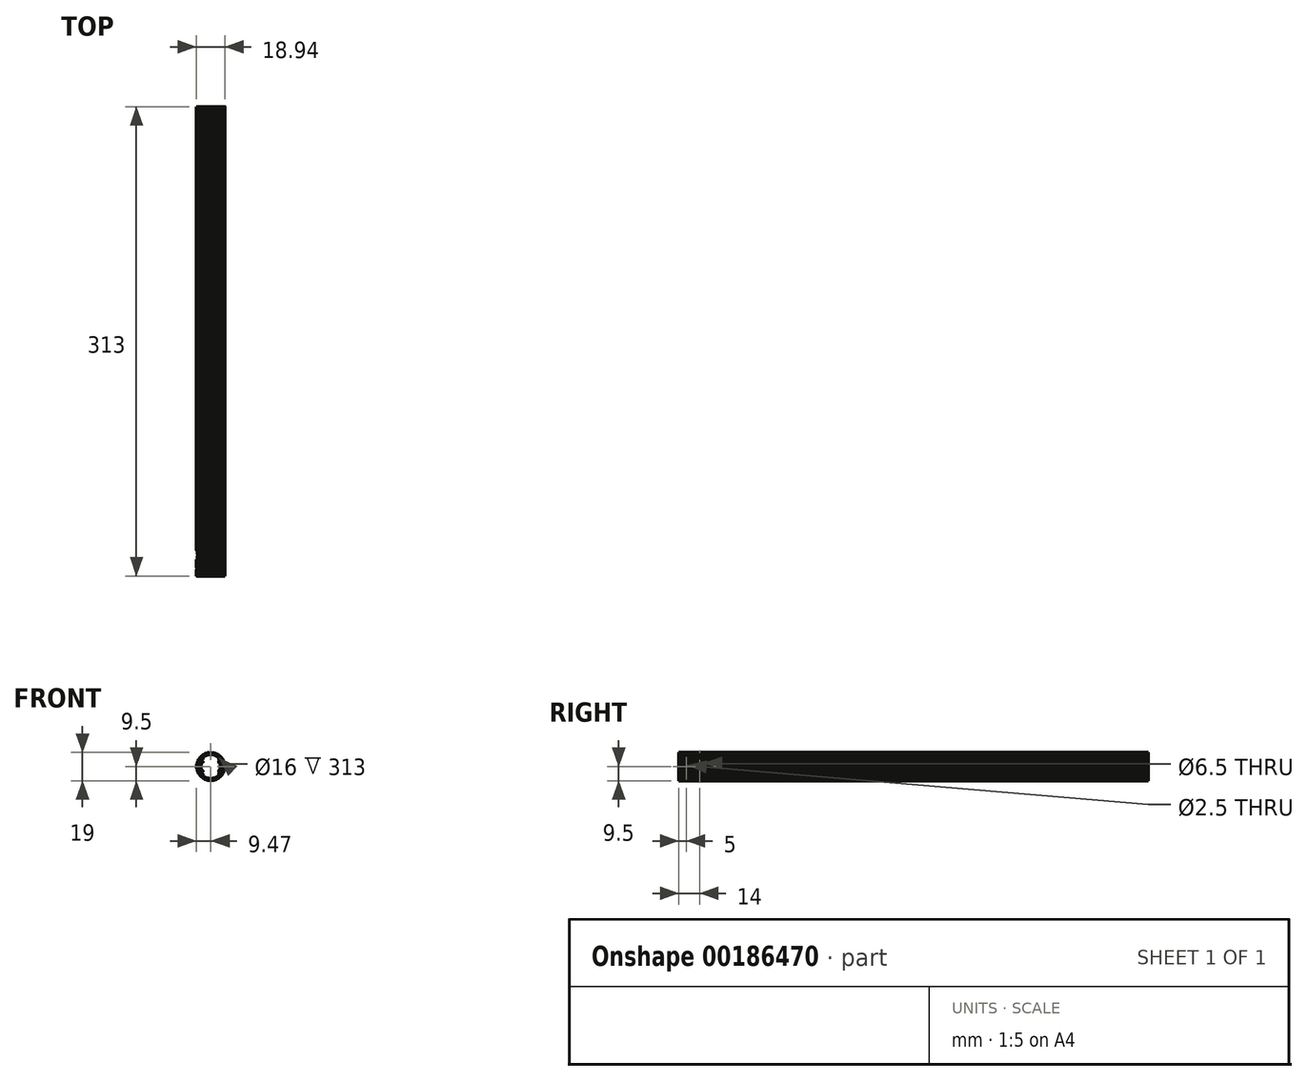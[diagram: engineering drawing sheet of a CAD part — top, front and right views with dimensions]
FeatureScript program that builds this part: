
annotation { "Feature Type Name" : "Feature", "Feature Type Description" : "" }
export const myFeature = defineFeature(function(context is Context, id is Id, definition is map)
    precondition{}
    {
        {
            assignVariable(context, id + "F0", {"name" : "Main_Diam", "anyValue" : 19});
        }
        {
            assignVariable(context, id + "F1", {"name" : "Main_Length", "anyValue" : 313});
        }
        {
            assignVariable(context, id + "F2", {"name" : "Bore_Depth_F", "anyValue" : 61});
        }
        {
            assignVariable(context, id + "F3", {"name" : "Bore_Depth_R", "anyValue" : 31});
        }
        {
            var Q0;
            Q0=qCreatedBy(makeId("Front.planeOp"),FACE);
            var sketch = newSketch(context, id + "F4", { "sketchPlane" : qUnion([Q0])});
            skLineSegment(sketch, "E0", {"start": v(-5.25, -3.45) * mm, "end": v(-5.25, -2.65) * mm});
            skLineSegment(sketch, "E1", {"start": v(9.2, 1.38) * mm, "end": v(9.42, 1.2) * mm});
            skArc(sketch, "E2", {"start": v(-5.35, -2.55) * mm, "mid": v(-5.28, -2.58) * mm, "end": v(-5.25, -2.65) * mm});
            skArc(sketch, "E3", {"start": v(6.3, 4.75) * mm, "mid": v(6.37, 4.72) * mm, "end": v(6.4, 4.65) * mm});
            skArc(sketch, "E4", {"start": v(-5.25, -6.04) * mm, "mid": v(0, -8) * mm, "end": v(5.25, -6.04) * mm});
            skLineSegment(sketch, "E5", {"start": v(1.53, 9.17) * mm, "end": v(1.78, 9.33) * mm});
            skLineSegment(sketch, "E6", {"start": v(-7.18, -5.91) * mm, "end": v(-7.2, -6.2) * mm});
            skArc(sketch, "E7", {"start": v(-8.33, -4.58) * mm, "mid": v(-8.23, -4.75) * mm, "end": v(-8.13, -4.92) * mm});
            skLineSegment(sketch, "E8", {"start": v(5.13, 7.76) * mm, "end": v(5.42, 7.8) * mm});
            skLineSegment(sketch, "E9", {"start": v(6.4, -2.45) * mm, "end": v(6.4, 0) * mm});
            skLineSegment(sketch, "E10", {"start": v(-2.33, -9) * mm, "end": v(-2.17, -9.25) * mm});
            skArc(sketch, "E11", {"start": v(8.97, -3.13) * mm, "mid": v(9.04, -2.94) * mm, "end": v(9.1, -2.74) * mm});
            skArc(sketch, "E12", {"start": v(-4.05, -8.6) * mm, "mid": v(-3.86, -8.68) * mm, "end": v(-3.68, -8.76) * mm});
            skArc(sketch, "E13", {"start": v(4.05, 8.6) * mm, "mid": v(3.86, 8.68) * mm, "end": v(3.68, 8.76) * mm});
            skLineSegment(sketch, "E14", {"start": v(6.63, 6.52) * mm, "end": v(6.92, 6.5) * mm});
            skArc(sketch, "E15", {"start": v(-6.4, 3.65) * mm, "mid": v(-6.37, 3.58) * mm, "end": v(-6.3, 3.55) * mm});
            skArc(sketch, "E16", {"start": v(5.74, 7.57) * mm, "mid": v(5.58, 7.69) * mm, "end": v(5.42, 7.8) * mm});
            skLineSegment(sketch, "E17", {"start": v(-9.2, 1.38) * mm, "end": v(-9.42, 1.2) * mm});
            skArc(sketch, "E18", {"start": v(1.78, -9.33) * mm, "mid": v(1.98, -9.3) * mm, "end": v(2.17, -9.25) * mm});
            skLineSegment(sketch, "E19", {"start": v(-5.8, 7.28) * mm, "end": v(-5.74, 7.57) * mm});
            skArc(sketch, "E20", {"start": v(-2.17, -9.25) * mm, "mid": v(-1.98, -9.3) * mm, "end": v(-1.78, -9.33) * mm});
            skLineSegment(sketch, "E21", {"start": v(7.84, 5) * mm, "end": v(8.13, 4.92) * mm});
            skLineSegment(sketch, "E22", {"start": v(2.33, 9) * mm, "end": v(2.17, 9.25) * mm});
            skArc(sketch, "E23", {"start": v(5.25, -3.45) * mm, "mid": v(5.28, -3.52) * mm, "end": v(5.35, -3.55) * mm});
            skLineSegment(sketch, "E24", {"start": v(5.8, -7.28) * mm, "end": v(5.74, -7.57) * mm});
            skArc(sketch, "E25", {"start": v(5.35, 2.55) * mm, "mid": v(5.28, 2.58) * mm, "end": v(5.25, 2.65) * mm});
            skArc(sketch, "E26", {"start": v(4.15, -8.32) * mm, "mid": v(4.65, -8.05) * mm, "end": v(5.13, -7.76) * mm});
            skArc(sketch, "E27", {"start": v(-5.35, 4.75) * mm, "mid": v(-5.28, 4.78) * mm, "end": v(-5.25, 4.85) * mm});
            skArc(sketch, "E28", {"start": v(-8.13, 4.92) * mm, "mid": v(-8.23, 4.75) * mm, "end": v(-8.33, 4.58) * mm});
            skLineSegment(sketch, "E29", {"start": v(7.84, -5) * mm, "end": v(8.13, -4.92) * mm});
            skArc(sketch, "E30", {"start": v(8.33, 4.58) * mm, "mid": v(8.23, 4.75) * mm, "end": v(8.13, 4.92) * mm});
            skLineSegment(sketch, "E31", {"start": v(-6.3, 3.55) * mm, "end": v(-5.35, 3.55) * mm});
            skLineSegment(sketch, "E32", {"start": v(-5.25, 3.45) * mm, "end": v(-5.25, 2.65) * mm});
            skArc(sketch, "E33", {"start": v(9.1, 2.74) * mm, "mid": v(9.04, 2.94) * mm, "end": v(8.97, 3.13) * mm});
            skLineSegment(sketch, "E34", {"start": v(6.3, 3.55) * mm, "end": v(5.35, 3.55) * mm});
            skLineSegment(sketch, "E35", {"start": v(4.15, -8.32) * mm, "end": v(4.05, -8.6) * mm});
            skLineSegment(sketch, "E36", {"start": v(5.25, 6.04) * mm, "end": v(5.25, 4.85) * mm});
            skArc(sketch, "E37", {"start": v(8.71, 3.26) * mm, "mid": v(8.5, 3.78) * mm, "end": v(8.25, 4.3) * mm});
            skArc(sketch, "E38", {"start": v(0.4, -9.3) * mm, "mid": v(0.97, -9.25) * mm, "end": v(1.53, -9.17) * mm});
            skArc(sketch, "E39", {"start": v(9.47, 0.8) * mm, "mid": v(9.45, 1) * mm, "end": v(9.42, 1.2) * mm});
            skArc(sketch, "E40", {"start": v(-4.15, 8.32) * mm, "mid": v(-4.65, 8.05) * mm, "end": v(-5.13, 7.76) * mm});
            skLineSegment(sketch, "E41", {"start": v(-0.4, 9.3) * mm, "end": v(-0.2, 9.5) * mm});
            skLineSegment(sketch, "E42", {"start": v(8.25, 4.3) * mm, "end": v(8.33, 4.58) * mm});
            skLineSegment(sketch, "E43", {"start": v(2.33, -9) * mm, "end": v(2.17, -9.25) * mm});
            skArc(sketch, "E44", {"start": v(-0.4, 9.3) * mm, "mid": v(-0.97, 9.25) * mm, "end": v(-1.53, 9.17) * mm});
            skLineSegment(sketch, "E45", {"start": v(-5.13, 7.76) * mm, "end": v(-5.42, 7.8) * mm});
            skLineSegment(sketch, "E46", {"start": v(-2.33, 9) * mm, "end": v(-2.17, 9.25) * mm});
            skLineSegment(sketch, "E47", {"start": v(6.63, -6.52) * mm, "end": v(6.92, -6.5) * mm});
            skArc(sketch, "E48", {"start": v(9.42, -1.2) * mm, "mid": v(9.45, -1) * mm, "end": v(9.47, -0.8) * mm});
            skArc(sketch, "E49", {"start": v(-3.68, 8.76) * mm, "mid": v(-3.86, 8.68) * mm, "end": v(-4.05, 8.6) * mm});
            skArc(sketch, "E50", {"start": v(9.2, 1.38) * mm, "mid": v(9.1, 1.93) * mm, "end": v(8.96, 2.48) * mm});
            skArc(sketch, "E51", {"start": v(5.35, 4.75) * mm, "mid": v(5.28, 4.78) * mm, "end": v(5.25, 4.85) * mm});
            skLineSegment(sketch, "E52", {"start": v(5.25, 3.45) * mm, "end": v(5.25, 2.65) * mm});
            skArc(sketch, "E53", {"start": v(-0.2, -9.5) * mm, "mid": v(0, -9.5) * mm, "end": v(0.2, -9.5) * mm});
            skArc(sketch, "E54", {"start": v(7.2, 6.2) * mm, "mid": v(7.06, 6.36) * mm, "end": v(6.92, 6.5) * mm});
            skLineSegment(sketch, "E55", {"start": v(3.4, 8.65) * mm, "end": v(3.68, 8.76) * mm});
            skArc(sketch, "E56", {"start": v(6.4, 3.65) * mm, "mid": v(6.37, 3.58) * mm, "end": v(6.3, 3.55) * mm});
            skLineSegment(sketch, "E57", {"start": v(-6.4, -2.45) * mm, "end": v(-6.4, 0) * mm});
            skArc(sketch, "E58", {"start": v(-2.33, 9) * mm, "mid": v(-2.87, 8.84) * mm, "end": v(-3.4, 8.65) * mm});
            skLineSegment(sketch, "E59", {"start": v(-1.53, 9.17) * mm, "end": v(-1.78, 9.33) * mm});
            skLineSegment(sketch, "E60", {"start": v(0.4, -9.3) * mm, "end": v(0.2, -9.5) * mm});
            skArc(sketch, "E61", {"start": v(-6.92, 6.5) * mm, "mid": v(-7.06, 6.36) * mm, "end": v(-7.2, 6.2) * mm});
            skArc(sketch, "E62", {"start": v(-8.25, 4.3) * mm, "mid": v(-8.5, 3.78) * mm, "end": v(-8.71, 3.26) * mm});
            skArc(sketch, "E63", {"start": v(6.3, -4.75) * mm, "mid": v(6.37, -4.72) * mm, "end": v(6.4, -4.65) * mm});
            skLineSegment(sketch, "E64", {"start": v(-6.4, 4.65) * mm, "end": v(-6.4, 3.65) * mm});
            skLineSegment(sketch, "E65", {"start": v(-6.4, 2.45) * mm, "end": v(-6.4, 0) * mm});
            skArc(sketch, "E66", {"start": v(8.25, -4.3) * mm, "mid": v(8.5, -3.78) * mm, "end": v(8.71, -3.26) * mm});
            skArc(sketch, "E67", {"start": v(-6.3, 2.55) * mm, "mid": v(-6.37, 2.52) * mm, "end": v(-6.4, 2.45) * mm});
            skLineSegment(sketch, "E68", {"start": v(-5.25, 6.04) * mm, "end": v(-5.25, 4.85) * mm});
            skLineSegment(sketch, "E69", {"start": v(-5.35, 4.75) * mm, "end": v(-6.3, 4.75) * mm});
            skLineSegment(sketch, "E70", {"start": v(-5.35, 2.55) * mm, "end": v(-6.3, 2.55) * mm});
            skArc(sketch, "E71", {"start": v(-5.25, 3.45) * mm, "mid": v(-5.28, 3.52) * mm, "end": v(-5.35, 3.55) * mm});
            skArc(sketch, "E72", {"start": v(-5.35, 2.55) * mm, "mid": v(-5.28, 2.58) * mm, "end": v(-5.25, 2.65) * mm});
            skArc(sketch, "E73", {"start": v(-6.3, 4.75) * mm, "mid": v(-6.37, 4.72) * mm, "end": v(-6.4, 4.65) * mm});
            skArc(sketch, "E74", {"start": v(6.3, 2.55) * mm, "mid": v(6.37, 2.52) * mm, "end": v(6.4, 2.45) * mm});
            skLineSegment(sketch, "E75", {"start": v(5.35, 2.55) * mm, "end": v(6.3, 2.55) * mm});
            skArc(sketch, "E76", {"start": v(5.25, 3.45) * mm, "mid": v(5.28, 3.52) * mm, "end": v(5.35, 3.55) * mm});
            skArc(sketch, "E77", {"start": v(0.2, 9.5) * mm, "mid": v(0, 9.5) * mm, "end": v(-0.2, 9.5) * mm});
            skLineSegment(sketch, "E78", {"start": v(5.35, 4.75) * mm, "end": v(6.3, 4.75) * mm});
            skLineSegment(sketch, "E79", {"start": v(6.4, 2.45) * mm, "end": v(6.4, 0) * mm});
            skLineSegment(sketch, "E80", {"start": v(6.4, 4.65) * mm, "end": v(6.4, 3.65) * mm});
            skArc(sketch, "E81", {"start": v(-5.35, -4.75) * mm, "mid": v(-5.28, -4.78) * mm, "end": v(-5.25, -4.85) * mm});
            skLineSegment(sketch, "E82", {"start": v(-6.3, -3.55) * mm, "end": v(-5.35, -3.55) * mm});
            skLineSegment(sketch, "E83", {"start": v(-5.35, -2.55) * mm, "end": v(-6.3, -2.55) * mm});
            skArc(sketch, "E84", {"start": v(-5.25, -3.45) * mm, "mid": v(-5.28, -3.52) * mm, "end": v(-5.35, -3.55) * mm});
            skArc(sketch, "E85", {"start": v(-6.3, -2.55) * mm, "mid": v(-6.37, -2.52) * mm, "end": v(-6.4, -2.45) * mm});
            skArc(sketch, "E86", {"start": v(-6.4, -3.65) * mm, "mid": v(-6.37, -3.58) * mm, "end": v(-6.3, -3.55) * mm});
            skArc(sketch, "E87", {"start": v(-6.3, -4.75) * mm, "mid": v(-6.37, -4.72) * mm, "end": v(-6.4, -4.65) * mm});
            skArc(sketch, "E88", {"start": v(5.35, -2.55) * mm, "mid": v(5.28, -2.58) * mm, "end": v(5.25, -2.65) * mm});
            skLineSegment(sketch, "E89", {"start": v(-3.4, 8.65) * mm, "end": v(-3.68, 8.76) * mm});
            skArc(sketch, "E90", {"start": v(6.3, -2.55) * mm, "mid": v(6.37, -2.52) * mm, "end": v(6.4, -2.45) * mm});
            skLineSegment(sketch, "E91", {"start": v(5.35, -2.55) * mm, "end": v(6.3, -2.55) * mm});
            skArc(sketch, "E92", {"start": v(6.4, -3.65) * mm, "mid": v(6.37, -3.58) * mm, "end": v(6.3, -3.55) * mm});
            skLineSegment(sketch, "E93", {"start": v(6.3, -3.55) * mm, "end": v(5.35, -3.55) * mm});
            skArc(sketch, "E94", {"start": v(5.35, -4.75) * mm, "mid": v(5.28, -4.78) * mm, "end": v(5.25, -4.85) * mm});
            skLineSegment(sketch, "E95", {"start": v(-5.25, -6.04) * mm, "end": v(-5.25, -4.85) * mm});
            skLineSegment(sketch, "E96", {"start": v(5.25, -3.45) * mm, "end": v(5.25, -2.65) * mm});
            skLineSegment(sketch, "E97", {"start": v(6.4, -4.65) * mm, "end": v(6.4, -3.65) * mm});
            skLineSegment(sketch, "E98", {"start": v(-5.35, -4.75) * mm, "end": v(-6.3, -4.75) * mm});
            skArc(sketch, "E99", {"start": v(-8.97, 3.13) * mm, "mid": v(-9.04, 2.94) * mm, "end": v(-9.1, 2.74) * mm});
            skLineSegment(sketch, "E100", {"start": v(-6.4, -4.65) * mm, "end": v(-6.4, -3.65) * mm});
            skLineSegment(sketch, "E101", {"start": v(5.35, -4.75) * mm, "end": v(6.3, -4.75) * mm});
            skLineSegment(sketch, "E102", {"start": v(-7.84, 5) * mm, "end": v(-8.13, 4.92) * mm});
            skLineSegment(sketch, "E103", {"start": v(5.25, -6.04) * mm, "end": v(5.25, -4.85) * mm});
            skArc(sketch, "E104", {"start": v(5.25, 6.04) * mm, "mid": v(0, 8) * mm, "end": v(-5.25, 6.04) * mm});
            skLineSegment(sketch, "E105", {"start": v(-0.4, -9.3) * mm, "end": v(-0.2, -9.5) * mm});
            skArc(sketch, "E106", {"start": v(2.33, -9) * mm, "mid": v(2.87, -8.84) * mm, "end": v(3.4, -8.65) * mm});
            skLineSegment(sketch, "E107", {"start": v(1.53, -9.17) * mm, "end": v(1.78, -9.33) * mm});
            skArc(sketch, "E108", {"start": v(3.68, -8.76) * mm, "mid": v(3.86, -8.68) * mm, "end": v(4.05, -8.6) * mm});
            skArc(sketch, "E109", {"start": v(-9.1, -2.74) * mm, "mid": v(-9.04, -2.94) * mm, "end": v(-8.97, -3.13) * mm});
            skLineSegment(sketch, "E110", {"start": v(3.4, -8.65) * mm, "end": v(3.68, -8.76) * mm});
            skArc(sketch, "E111", {"start": v(5.8, -7.28) * mm, "mid": v(6.22, -6.91) * mm, "end": v(6.63, -6.52) * mm});
            skArc(sketch, "E112", {"start": v(5.42, -7.8) * mm, "mid": v(5.58, -7.69) * mm, "end": v(5.74, -7.57) * mm});
            skLineSegment(sketch, "E113", {"start": v(5.13, -7.76) * mm, "end": v(5.42, -7.8) * mm});
            skLineSegment(sketch, "E114", {"start": v(-5.13, -7.76) * mm, "end": v(-5.42, -7.8) * mm});
            skLineSegment(sketch, "E115", {"start": v(7.18, -5.91) * mm, "end": v(7.2, -6.2) * mm});
            skLineSegment(sketch, "E116", {"start": v(-6.63, -6.52) * mm, "end": v(-6.92, -6.5) * mm});
            skArc(sketch, "E117", {"start": v(8.13, -4.92) * mm, "mid": v(8.23, -4.75) * mm, "end": v(8.33, -4.58) * mm});
            skArc(sketch, "E118", {"start": v(6.92, -6.5) * mm, "mid": v(7.06, -6.36) * mm, "end": v(7.2, -6.2) * mm});
            skArc(sketch, "E119", {"start": v(-5.74, -7.57) * mm, "mid": v(-5.58, -7.69) * mm, "end": v(-5.42, -7.8) * mm});
            skArc(sketch, "E120", {"start": v(8.96, -2.48) * mm, "mid": v(9.1, -1.93) * mm, "end": v(9.2, -1.38) * mm});
            skLineSegment(sketch, "E121", {"start": v(8.96, -2.48) * mm, "end": v(9.1, -2.74) * mm});
            skLineSegment(sketch, "E122", {"start": v(8.71, -3.26) * mm, "end": v(8.97, -3.13) * mm});
            skArc(sketch, "E123", {"start": v(9.28, -0.57) * mm, "mid": v(9.3, 0) * mm, "end": v(9.28, 0.57) * mm});
            skLineSegment(sketch, "E124", {"start": v(9.28, -0.57) * mm, "end": v(9.47, -0.8) * mm});
            skLineSegment(sketch, "E125", {"start": v(-1.53, -9.17) * mm, "end": v(-1.78, -9.33) * mm});
            skLineSegment(sketch, "E126", {"start": v(9.2, -1.38) * mm, "end": v(9.42, -1.2) * mm});
            skLineSegment(sketch, "E127", {"start": v(8.71, 3.26) * mm, "end": v(8.97, 3.13) * mm});
            skLineSegment(sketch, "E128", {"start": v(8.96, 2.48) * mm, "end": v(9.1, 2.74) * mm});
            skArc(sketch, "E129", {"start": v(7.84, 5) * mm, "mid": v(7.52, 5.47) * mm, "end": v(7.18, 5.91) * mm});
            skArc(sketch, "E130", {"start": v(6.63, 6.52) * mm, "mid": v(6.22, 6.91) * mm, "end": v(5.8, 7.28) * mm});
            skLineSegment(sketch, "E131", {"start": v(7.18, 5.91) * mm, "end": v(7.2, 6.2) * mm});
            skArc(sketch, "E132", {"start": v(5.13, 7.76) * mm, "mid": v(4.65, 8.05) * mm, "end": v(4.15, 8.32) * mm});
            skLineSegment(sketch, "E133", {"start": v(5.8, 7.28) * mm, "end": v(5.74, 7.57) * mm});
            skArc(sketch, "E134", {"start": v(3.4, 8.65) * mm, "mid": v(2.87, 8.84) * mm, "end": v(2.33, 9) * mm});
            skLineSegment(sketch, "E135", {"start": v(4.15, 8.32) * mm, "end": v(4.05, 8.6) * mm});
            skArc(sketch, "E136", {"start": v(1.53, 9.17) * mm, "mid": v(0.97, 9.25) * mm, "end": v(0.4, 9.3) * mm});
            skArc(sketch, "E137", {"start": v(2.17, 9.25) * mm, "mid": v(1.98, 9.3) * mm, "end": v(1.78, 9.33) * mm});
            skLineSegment(sketch, "E138", {"start": v(0.4, 9.3) * mm, "end": v(0.2, 9.5) * mm});
            skArc(sketch, "E139", {"start": v(-1.78, 9.33) * mm, "mid": v(-1.98, 9.3) * mm, "end": v(-2.17, 9.25) * mm});
            skLineSegment(sketch, "E140", {"start": v(-4.15, 8.32) * mm, "end": v(-4.05, 8.6) * mm});
            skArc(sketch, "E141", {"start": v(-5.8, 7.28) * mm, "mid": v(-6.22, 6.91) * mm, "end": v(-6.63, 6.52) * mm});
            skArc(sketch, "E142", {"start": v(-5.42, 7.8) * mm, "mid": v(-5.58, 7.69) * mm, "end": v(-5.74, 7.57) * mm});
            skLineSegment(sketch, "E143", {"start": v(-9.2, -1.38) * mm, "end": v(-9.42, -1.2) * mm});
            skLineSegment(sketch, "E144", {"start": v(-7.18, 5.91) * mm, "end": v(-7.2, 6.2) * mm});
            skLineSegment(sketch, "E145", {"start": v(-6.63, 6.52) * mm, "end": v(-6.92, 6.5) * mm});
            skArc(sketch, "E146", {"start": v(-8.96, 2.48) * mm, "mid": v(-9.1, 1.93) * mm, "end": v(-9.2, 1.38) * mm});
            skLineSegment(sketch, "E147", {"start": v(-8.96, 2.48) * mm, "end": v(-9.1, 2.74) * mm});
            skLineSegment(sketch, "E148", {"start": v(-8.71, 3.26) * mm, "end": v(-8.97, 3.13) * mm});
            skArc(sketch, "E149", {"start": v(-9.28, 0.57) * mm, "mid": v(-9.3, 0) * mm, "end": v(-9.28, -0.57) * mm});
            skArc(sketch, "E150", {"start": v(-9.42, 1.2) * mm, "mid": v(-9.45, 1) * mm, "end": v(-9.47, 0.8) * mm});
            skLineSegment(sketch, "E151", {"start": v(-9.28, 0.57) * mm, "end": v(-9.47, 0.8) * mm});
            skLineSegment(sketch, "E152", {"start": v(8.25, -4.3) * mm, "end": v(8.33, -4.58) * mm});
            skArc(sketch, "E153", {"start": v(-9.2, -1.38) * mm, "mid": v(-9.1, -1.93) * mm, "end": v(-8.96, -2.48) * mm});
            skArc(sketch, "E154", {"start": v(-9.47, -0.8) * mm, "mid": v(-9.45, -1) * mm, "end": v(-9.42, -1.2) * mm});
            skLineSegment(sketch, "E155", {"start": v(-9.28, -0.57) * mm, "end": v(-9.47, -0.8) * mm});
            skArc(sketch, "E156", {"start": v(-8.71, -3.26) * mm, "mid": v(-8.5, -3.78) * mm, "end": v(-8.25, -4.3) * mm});
            skLineSegment(sketch, "E157", {"start": v(-8.71, -3.26) * mm, "end": v(-8.97, -3.13) * mm});
            skLineSegment(sketch, "E158", {"start": v(-8.96, -2.48) * mm, "end": v(-9.1, -2.74) * mm});
            skArc(sketch, "E159", {"start": v(-7.84, -5) * mm, "mid": v(-7.52, -5.47) * mm, "end": v(-7.18, -5.91) * mm});
            skLineSegment(sketch, "E160", {"start": v(-7.84, -5) * mm, "end": v(-8.13, -4.92) * mm});
            skLineSegment(sketch, "E161", {"start": v(-8.25, -4.3) * mm, "end": v(-8.33, -4.58) * mm});
            skArc(sketch, "E162", {"start": v(-6.63, -6.52) * mm, "mid": v(-6.22, -6.91) * mm, "end": v(-5.8, -7.28) * mm});
            skLineSegment(sketch, "E163", {"start": v(9.28, 0.57) * mm, "end": v(9.47, 0.8) * mm});
            skArc(sketch, "E164", {"start": v(-7.2, -6.2) * mm, "mid": v(-7.06, -6.36) * mm, "end": v(-6.92, -6.5) * mm});
            skArc(sketch, "E165", {"start": v(7.18, -5.91) * mm, "mid": v(7.52, -5.47) * mm, "end": v(7.84, -5) * mm});
            skLineSegment(sketch, "E166", {"start": v(-5.8, -7.28) * mm, "end": v(-5.74, -7.57) * mm});
            skArc(sketch, "E167", {"start": v(-3.4, -8.65) * mm, "mid": v(-2.87, -8.84) * mm, "end": v(-2.33, -9) * mm});
            skLineSegment(sketch, "E168", {"start": v(-3.4, -8.65) * mm, "end": v(-3.68, -8.76) * mm});
            skLineSegment(sketch, "E169", {"start": v(-4.15, -8.32) * mm, "end": v(-4.05, -8.6) * mm});
            skArc(sketch, "E170", {"start": v(-1.53, -9.17) * mm, "mid": v(-0.97, -9.25) * mm, "end": v(-0.4, -9.3) * mm});
            skArc(sketch, "E171", {"start": v(-7.18, 5.91) * mm, "mid": v(-7.52, 5.47) * mm, "end": v(-7.84, 5) * mm});
            skLineSegment(sketch, "E172", {"start": v(-8.25, 4.3) * mm, "end": v(-8.33, 4.58) * mm});
            skArc(sketch, "E173", {"start": v(-5.13, -7.76) * mm, "mid": v(-4.65, -8.05) * mm, "end": v(-4.15, -8.32) * mm});
            skSolve(sketch);
        }
        {
            var Q0;
            Q0=makeQuery(id+"F4.imprint","IMPRINT",FACE,{"disambiguationData":[TD([[makeQuery(id+"F4.imprint","IMPRINT",EDGE,{"derivedFrom":sQuery(id+"F4.wireOp",EDGE,"E0")}),1.0]])]});
            extrude(context, id + "F5", {"entities" : qUnion([Q0]), "depth" : (getVariable(context, 'Main_Length') - getVariable(context, 'Bore_Depth_F') - getVariable(context, 'Bore_Depth_R')) * mm});
        }
        {
            var Q0;
            Q0=makeQuery(id+"F5.opExtrude","CAP_FACE",FACE,{"disambiguationData":[OSD([sQuery(id+"F4.wireOp",EDGE,"E0"),sQuery(id+"F4.wireOp",EDGE,"E1"),sQuery(id+"F4.wireOp",EDGE,"E2"),sQuery(id+"F4.wireOp",EDGE,"E3"),sQuery(id+"F4.wireOp",EDGE,"E4"),sQuery(id+"F4.wireOp",EDGE,"E5"),sQuery(id+"F4.wireOp",EDGE,"E6"),sQuery(id+"F4.wireOp",EDGE,"E7"),sQuery(id+"F4.wireOp",EDGE,"E8"),sQuery(id+"F4.wireOp",EDGE,"E9"),sQuery(id+"F4.wireOp",EDGE,"E10"),sQuery(id+"F4.wireOp",EDGE,"E11"),sQuery(id+"F4.wireOp",EDGE,"E12"),sQuery(id+"F4.wireOp",EDGE,"E13"),sQuery(id+"F4.wireOp",EDGE,"E14"),sQuery(id+"F4.wireOp",EDGE,"E15"),sQuery(id+"F4.wireOp",EDGE,"E16"),sQuery(id+"F4.wireOp",EDGE,"E17"),sQuery(id+"F4.wireOp",EDGE,"E18"),sQuery(id+"F4.wireOp",EDGE,"E19"),sQuery(id+"F4.wireOp",EDGE,"E20"),sQuery(id+"F4.wireOp",EDGE,"E21"),sQuery(id+"F4.wireOp",EDGE,"E22"),sQuery(id+"F4.wireOp",EDGE,"E23"),sQuery(id+"F4.wireOp",EDGE,"E24"),sQuery(id+"F4.wireOp",EDGE,"E25"),sQuery(id+"F4.wireOp",EDGE,"E26"),sQuery(id+"F4.wireOp",EDGE,"E27"),sQuery(id+"F4.wireOp",EDGE,"E28"),sQuery(id+"F4.wireOp",EDGE,"E29"),sQuery(id+"F4.wireOp",EDGE,"E30"),sQuery(id+"F4.wireOp",EDGE,"E31"),sQuery(id+"F4.wireOp",EDGE,"E32"),sQuery(id+"F4.wireOp",EDGE,"E33"),sQuery(id+"F4.wireOp",EDGE,"E34"),sQuery(id+"F4.wireOp",EDGE,"E35"),sQuery(id+"F4.wireOp",EDGE,"E36"),sQuery(id+"F4.wireOp",EDGE,"E37"),sQuery(id+"F4.wireOp",EDGE,"E38"),sQuery(id+"F4.wireOp",EDGE,"E39"),sQuery(id+"F4.wireOp",EDGE,"E40"),sQuery(id+"F4.wireOp",EDGE,"E41"),sQuery(id+"F4.wireOp",EDGE,"E42"),sQuery(id+"F4.wireOp",EDGE,"E43"),sQuery(id+"F4.wireOp",EDGE,"E44"),sQuery(id+"F4.wireOp",EDGE,"E45"),sQuery(id+"F4.wireOp",EDGE,"E46"),sQuery(id+"F4.wireOp",EDGE,"E47"),sQuery(id+"F4.wireOp",EDGE,"E48"),sQuery(id+"F4.wireOp",EDGE,"E49"),sQuery(id+"F4.wireOp",EDGE,"E50"),sQuery(id+"F4.wireOp",EDGE,"E51"),sQuery(id+"F4.wireOp",EDGE,"E52"),sQuery(id+"F4.wireOp",EDGE,"E53"),sQuery(id+"F4.wireOp",EDGE,"E54"),sQuery(id+"F4.wireOp",EDGE,"E55"),sQuery(id+"F4.wireOp",EDGE,"E56"),sQuery(id+"F4.wireOp",EDGE,"E57"),sQuery(id+"F4.wireOp",EDGE,"E58"),sQuery(id+"F4.wireOp",EDGE,"E59"),sQuery(id+"F4.wireOp",EDGE,"E60"),sQuery(id+"F4.wireOp",EDGE,"E61"),sQuery(id+"F4.wireOp",EDGE,"E62"),sQuery(id+"F4.wireOp",EDGE,"E63"),sQuery(id+"F4.wireOp",EDGE,"E64"),sQuery(id+"F4.wireOp",EDGE,"E65"),sQuery(id+"F4.wireOp",EDGE,"E66"),sQuery(id+"F4.wireOp",EDGE,"E67"),sQuery(id+"F4.wireOp",EDGE,"E68"),sQuery(id+"F4.wireOp",EDGE,"E69"),sQuery(id+"F4.wireOp",EDGE,"E70"),sQuery(id+"F4.wireOp",EDGE,"E71"),sQuery(id+"F4.wireOp",EDGE,"E72"),sQuery(id+"F4.wireOp",EDGE,"E73"),sQuery(id+"F4.wireOp",EDGE,"E74"),sQuery(id+"F4.wireOp",EDGE,"E75"),sQuery(id+"F4.wireOp",EDGE,"E76"),sQuery(id+"F4.wireOp",EDGE,"E77"),sQuery(id+"F4.wireOp",EDGE,"E78"),sQuery(id+"F4.wireOp",EDGE,"E79"),sQuery(id+"F4.wireOp",EDGE,"E80"),sQuery(id+"F4.wireOp",EDGE,"E81"),sQuery(id+"F4.wireOp",EDGE,"E82"),sQuery(id+"F4.wireOp",EDGE,"E83"),sQuery(id+"F4.wireOp",EDGE,"E84"),sQuery(id+"F4.wireOp",EDGE,"E85"),sQuery(id+"F4.wireOp",EDGE,"E86"),sQuery(id+"F4.wireOp",EDGE,"E87"),sQuery(id+"F4.wireOp",EDGE,"E88"),sQuery(id+"F4.wireOp",EDGE,"E89"),sQuery(id+"F4.wireOp",EDGE,"E90"),sQuery(id+"F4.wireOp",EDGE,"E91"),sQuery(id+"F4.wireOp",EDGE,"E92"),sQuery(id+"F4.wireOp",EDGE,"E93"),sQuery(id+"F4.wireOp",EDGE,"E94"),sQuery(id+"F4.wireOp",EDGE,"E95"),sQuery(id+"F4.wireOp",EDGE,"E96"),sQuery(id+"F4.wireOp",EDGE,"E97"),sQuery(id+"F4.wireOp",EDGE,"E98"),sQuery(id+"F4.wireOp",EDGE,"E99"),sQuery(id+"F4.wireOp",EDGE,"E100"),sQuery(id+"F4.wireOp",EDGE,"E101"),sQuery(id+"F4.wireOp",EDGE,"E102"),sQuery(id+"F4.wireOp",EDGE,"E103"),sQuery(id+"F4.wireOp",EDGE,"E104"),sQuery(id+"F4.wireOp",EDGE,"E105"),sQuery(id+"F4.wireOp",EDGE,"E106"),sQuery(id+"F4.wireOp",EDGE,"E107"),sQuery(id+"F4.wireOp",EDGE,"E108"),sQuery(id+"F4.wireOp",EDGE,"E109"),sQuery(id+"F4.wireOp",EDGE,"E110"),sQuery(id+"F4.wireOp",EDGE,"E111"),sQuery(id+"F4.wireOp",EDGE,"E112"),sQuery(id+"F4.wireOp",EDGE,"E113"),sQuery(id+"F4.wireOp",EDGE,"E114"),sQuery(id+"F4.wireOp",EDGE,"E115"),sQuery(id+"F4.wireOp",EDGE,"E116"),sQuery(id+"F4.wireOp",EDGE,"E117"),sQuery(id+"F4.wireOp",EDGE,"E118"),sQuery(id+"F4.wireOp",EDGE,"E119"),sQuery(id+"F4.wireOp",EDGE,"E120"),sQuery(id+"F4.wireOp",EDGE,"E121"),sQuery(id+"F4.wireOp",EDGE,"E122"),sQuery(id+"F4.wireOp",EDGE,"E123"),sQuery(id+"F4.wireOp",EDGE,"E124"),sQuery(id+"F4.wireOp",EDGE,"E125"),sQuery(id+"F4.wireOp",EDGE,"E126"),sQuery(id+"F4.wireOp",EDGE,"E127"),sQuery(id+"F4.wireOp",EDGE,"E128"),sQuery(id+"F4.wireOp",EDGE,"E129"),sQuery(id+"F4.wireOp",EDGE,"E130"),sQuery(id+"F4.wireOp",EDGE,"E131"),sQuery(id+"F4.wireOp",EDGE,"E132"),sQuery(id+"F4.wireOp",EDGE,"E133"),sQuery(id+"F4.wireOp",EDGE,"E134"),sQuery(id+"F4.wireOp",EDGE,"E135"),sQuery(id+"F4.wireOp",EDGE,"E136"),sQuery(id+"F4.wireOp",EDGE,"E137"),sQuery(id+"F4.wireOp",EDGE,"E138"),sQuery(id+"F4.wireOp",EDGE,"E139"),sQuery(id+"F4.wireOp",EDGE,"E140"),sQuery(id+"F4.wireOp",EDGE,"E141"),sQuery(id+"F4.wireOp",EDGE,"E142"),sQuery(id+"F4.wireOp",EDGE,"E143"),sQuery(id+"F4.wireOp",EDGE,"E144"),sQuery(id+"F4.wireOp",EDGE,"E145"),sQuery(id+"F4.wireOp",EDGE,"E146"),sQuery(id+"F4.wireOp",EDGE,"E147"),sQuery(id+"F4.wireOp",EDGE,"E148"),sQuery(id+"F4.wireOp",EDGE,"E149"),sQuery(id+"F4.wireOp",EDGE,"E150"),sQuery(id+"F4.wireOp",EDGE,"E151"),sQuery(id+"F4.wireOp",EDGE,"E152"),sQuery(id+"F4.wireOp",EDGE,"E153"),sQuery(id+"F4.wireOp",EDGE,"E154"),sQuery(id+"F4.wireOp",EDGE,"E155"),sQuery(id+"F4.wireOp",EDGE,"E156"),sQuery(id+"F4.wireOp",EDGE,"E157"),sQuery(id+"F4.wireOp",EDGE,"E158"),sQuery(id+"F4.wireOp",EDGE,"E159"),sQuery(id+"F4.wireOp",EDGE,"E160"),sQuery(id+"F4.wireOp",EDGE,"E161"),sQuery(id+"F4.wireOp",EDGE,"E162"),sQuery(id+"F4.wireOp",EDGE,"E163"),sQuery(id+"F4.wireOp",EDGE,"E164"),sQuery(id+"F4.wireOp",EDGE,"E165"),sQuery(id+"F4.wireOp",EDGE,"E166"),sQuery(id+"F4.wireOp",EDGE,"E167"),sQuery(id+"F4.wireOp",EDGE,"E168"),sQuery(id+"F4.wireOp",EDGE,"E169"),sQuery(id+"F4.wireOp",EDGE,"E170"),sQuery(id+"F4.wireOp",EDGE,"E171"),sQuery(id+"F4.wireOp",EDGE,"E172"),sQuery(id+"F4.wireOp",EDGE,"E173")])],"isStart":false});
            var sketch = newSketch(context, id + "F6", { "sketchPlane" : qUnion([Q0])});
            skCircle(sketch, "E174", {"center": v(0, 0) * mm, "radius": 8 * mm});
            skLineSegment(sketch, "E175.0.0", {"start": v(9.42, 1.2) * mm, "end": v(9.2, 1.38) * mm});
            skArc(sketch, "E175.0.1", {"start": v(9.2, 1.38) * mm, "mid": v(9.1, 1.93) * mm, "end": v(8.96, 2.48) * mm});
            skLineSegment(sketch, "E175.0.2", {"start": v(8.96, 2.48) * mm, "end": v(9.1, 2.74) * mm});
            skArc(sketch, "E175.0.3", {"start": v(9.1, 2.74) * mm, "mid": v(9.04, 2.94) * mm, "end": v(8.97, 3.13) * mm});
            skLineSegment(sketch, "E175.0.4", {"start": v(8.97, 3.13) * mm, "end": v(8.71, 3.26) * mm});
            skArc(sketch, "E175.0.5", {"start": v(8.71, 3.26) * mm, "mid": v(8.5, 3.78) * mm, "end": v(8.25, 4.3) * mm});
            skLineSegment(sketch, "E175.0.6", {"start": v(8.25, 4.3) * mm, "end": v(8.33, 4.58) * mm});
            skArc(sketch, "E175.0.7", {"start": v(8.33, 4.58) * mm, "mid": v(8.23, 4.75) * mm, "end": v(8.13, 4.92) * mm});
            skLineSegment(sketch, "E175.0.8", {"start": v(8.13, 4.92) * mm, "end": v(7.84, 5) * mm});
            skArc(sketch, "E175.0.9", {"start": v(7.84, 5) * mm, "mid": v(7.52, 5.47) * mm, "end": v(7.18, 5.91) * mm});
            skLineSegment(sketch, "E175.0.10", {"start": v(7.18, 5.91) * mm, "end": v(7.2, 6.2) * mm});
            skArc(sketch, "E175.0.11", {"start": v(7.2, 6.2) * mm, "mid": v(7.06, 6.36) * mm, "end": v(6.92, 6.5) * mm});
            skLineSegment(sketch, "E175.0.12", {"start": v(6.92, 6.5) * mm, "end": v(6.63, 6.52) * mm});
            skArc(sketch, "E175.0.13", {"start": v(6.63, 6.52) * mm, "mid": v(6.22, 6.91) * mm, "end": v(5.8, 7.28) * mm});
            skLineSegment(sketch, "E175.0.14", {"start": v(5.8, 7.28) * mm, "end": v(5.74, 7.57) * mm});
            skArc(sketch, "E175.0.15", {"start": v(5.74, 7.57) * mm, "mid": v(5.58, 7.69) * mm, "end": v(5.42, 7.8) * mm});
            skLineSegment(sketch, "E175.0.16", {"start": v(5.42, 7.8) * mm, "end": v(5.13, 7.76) * mm});
            skArc(sketch, "E175.0.17", {"start": v(5.13, 7.76) * mm, "mid": v(4.65, 8.05) * mm, "end": v(4.15, 8.32) * mm});
            skLineSegment(sketch, "E175.0.18", {"start": v(4.15, 8.32) * mm, "end": v(4.05, 8.6) * mm});
            skArc(sketch, "E175.0.19", {"start": v(4.05, 8.6) * mm, "mid": v(3.86, 8.68) * mm, "end": v(3.68, 8.76) * mm});
            skLineSegment(sketch, "E175.0.20", {"start": v(3.68, 8.76) * mm, "end": v(3.4, 8.65) * mm});
            skArc(sketch, "E175.0.21", {"start": v(3.4, 8.65) * mm, "mid": v(2.87, 8.84) * mm, "end": v(2.33, 9) * mm});
            skLineSegment(sketch, "E175.0.22", {"start": v(2.33, 9) * mm, "end": v(2.17, 9.25) * mm});
            skArc(sketch, "E175.0.23", {"start": v(2.17, 9.25) * mm, "mid": v(1.98, 9.3) * mm, "end": v(1.78, 9.33) * mm});
            skLineSegment(sketch, "E175.0.24", {"start": v(1.78, 9.33) * mm, "end": v(1.53, 9.17) * mm});
            skArc(sketch, "E175.0.25", {"start": v(1.53, 9.17) * mm, "mid": v(0.97, 9.25) * mm, "end": v(0.4, 9.3) * mm});
            skLineSegment(sketch, "E175.0.26", {"start": v(0.4, 9.3) * mm, "end": v(0.2, 9.5) * mm});
            skArc(sketch, "E175.0.27", {"start": v(0.2, 9.5) * mm, "mid": v(0, 9.5) * mm, "end": v(-0.2, 9.5) * mm});
            skLineSegment(sketch, "E175.0.28", {"start": v(-0.2, 9.5) * mm, "end": v(-0.4, 9.3) * mm});
            skArc(sketch, "E175.0.29", {"start": v(-0.4, 9.3) * mm, "mid": v(-0.97, 9.25) * mm, "end": v(-1.53, 9.17) * mm});
            skLineSegment(sketch, "E175.0.30", {"start": v(-1.53, 9.17) * mm, "end": v(-1.78, 9.33) * mm});
            skArc(sketch, "E175.0.31", {"start": v(-1.78, 9.33) * mm, "mid": v(-1.98, 9.3) * mm, "end": v(-2.17, 9.25) * mm});
            skLineSegment(sketch, "E175.0.32", {"start": v(-2.17, 9.25) * mm, "end": v(-2.33, 9) * mm});
            skArc(sketch, "E175.0.33", {"start": v(-2.33, 9) * mm, "mid": v(-2.87, 8.84) * mm, "end": v(-3.4, 8.65) * mm});
            skLineSegment(sketch, "E175.0.34", {"start": v(-3.4, 8.65) * mm, "end": v(-3.68, 8.76) * mm});
            skArc(sketch, "E175.0.35", {"start": v(-3.68, 8.76) * mm, "mid": v(-3.86, 8.68) * mm, "end": v(-4.05, 8.6) * mm});
            skLineSegment(sketch, "E175.0.36", {"start": v(-4.05, 8.6) * mm, "end": v(-4.15, 8.32) * mm});
            skArc(sketch, "E175.0.37", {"start": v(-4.15, 8.32) * mm, "mid": v(-4.65, 8.05) * mm, "end": v(-5.13, 7.76) * mm});
            skLineSegment(sketch, "E175.0.38", {"start": v(-5.13, 7.76) * mm, "end": v(-5.42, 7.8) * mm});
            skArc(sketch, "E175.0.39", {"start": v(-5.42, 7.8) * mm, "mid": v(-5.58, 7.69) * mm, "end": v(-5.74, 7.57) * mm});
            skLineSegment(sketch, "E175.0.40", {"start": v(-5.74, 7.57) * mm, "end": v(-5.8, 7.28) * mm});
            skArc(sketch, "E175.0.41", {"start": v(-5.8, 7.28) * mm, "mid": v(-6.22, 6.91) * mm, "end": v(-6.63, 6.52) * mm});
            skLineSegment(sketch, "E175.0.42", {"start": v(-6.63, 6.52) * mm, "end": v(-6.92, 6.5) * mm});
            skArc(sketch, "E175.0.43", {"start": v(-6.92, 6.5) * mm, "mid": v(-7.06, 6.36) * mm, "end": v(-7.2, 6.2) * mm});
            skLineSegment(sketch, "E175.0.44", {"start": v(-7.2, 6.2) * mm, "end": v(-7.18, 5.91) * mm});
            skArc(sketch, "E175.0.45", {"start": v(-7.18, 5.91) * mm, "mid": v(-7.52, 5.47) * mm, "end": v(-7.84, 5) * mm});
            skLineSegment(sketch, "E175.0.46", {"start": v(-7.84, 5) * mm, "end": v(-8.13, 4.92) * mm});
            skArc(sketch, "E175.0.47", {"start": v(-8.13, 4.92) * mm, "mid": v(-8.23, 4.75) * mm, "end": v(-8.33, 4.58) * mm});
            skLineSegment(sketch, "E175.0.48", {"start": v(-8.33, 4.58) * mm, "end": v(-8.25, 4.3) * mm});
            skArc(sketch, "E175.0.49", {"start": v(-8.25, 4.3) * mm, "mid": v(-8.5, 3.78) * mm, "end": v(-8.71, 3.26) * mm});
            skLineSegment(sketch, "E175.0.50", {"start": v(-8.71, 3.26) * mm, "end": v(-8.97, 3.13) * mm});
            skArc(sketch, "E175.0.51", {"start": v(-8.97, 3.13) * mm, "mid": v(-9.04, 2.94) * mm, "end": v(-9.1, 2.74) * mm});
            skLineSegment(sketch, "E175.0.52", {"start": v(-9.1, 2.74) * mm, "end": v(-8.96, 2.48) * mm});
            skArc(sketch, "E175.0.53", {"start": v(-8.96, 2.48) * mm, "mid": v(-9.1, 1.93) * mm, "end": v(-9.2, 1.38) * mm});
            skLineSegment(sketch, "E175.0.54", {"start": v(-9.2, 1.38) * mm, "end": v(-9.42, 1.2) * mm});
            skArc(sketch, "E175.0.55", {"start": v(-9.42, 1.2) * mm, "mid": v(-9.45, 1) * mm, "end": v(-9.47, 0.8) * mm});
            skLineSegment(sketch, "E175.0.56", {"start": v(-9.47, 0.8) * mm, "end": v(-9.28, 0.57) * mm});
            skArc(sketch, "E175.0.57", {"start": v(-9.28, 0.57) * mm, "mid": v(-9.3, 0) * mm, "end": v(-9.28, -0.57) * mm});
            skLineSegment(sketch, "E175.0.58", {"start": v(-9.28, -0.57) * mm, "end": v(-9.47, -0.8) * mm});
            skArc(sketch, "E175.0.59", {"start": v(-9.47, -0.8) * mm, "mid": v(-9.45, -1) * mm, "end": v(-9.42, -1.2) * mm});
            skLineSegment(sketch, "E175.0.60", {"start": v(-9.42, -1.2) * mm, "end": v(-9.2, -1.38) * mm});
            skArc(sketch, "E175.0.61", {"start": v(-9.2, -1.38) * mm, "mid": v(-9.1, -1.93) * mm, "end": v(-8.96, -2.48) * mm});
            skLineSegment(sketch, "E175.0.62", {"start": v(-8.96, -2.48) * mm, "end": v(-9.1, -2.74) * mm});
            skArc(sketch, "E175.0.63", {"start": v(-9.1, -2.74) * mm, "mid": v(-9.04, -2.94) * mm, "end": v(-8.97, -3.13) * mm});
            skLineSegment(sketch, "E175.0.64", {"start": v(-8.97, -3.13) * mm, "end": v(-8.71, -3.26) * mm});
            skArc(sketch, "E175.0.65", {"start": v(-8.71, -3.26) * mm, "mid": v(-8.5, -3.78) * mm, "end": v(-8.25, -4.3) * mm});
            skLineSegment(sketch, "E175.0.66", {"start": v(-8.25, -4.3) * mm, "end": v(-8.33, -4.58) * mm});
            skArc(sketch, "E175.0.67", {"start": v(-8.33, -4.58) * mm, "mid": v(-8.23, -4.75) * mm, "end": v(-8.13, -4.92) * mm});
            skLineSegment(sketch, "E175.0.68", {"start": v(-8.13, -4.92) * mm, "end": v(-7.84, -5) * mm});
            skArc(sketch, "E175.0.69", {"start": v(-7.84, -5) * mm, "mid": v(-7.52, -5.47) * mm, "end": v(-7.18, -5.91) * mm});
            skLineSegment(sketch, "E175.0.70", {"start": v(-7.18, -5.91) * mm, "end": v(-7.2, -6.2) * mm});
            skArc(sketch, "E175.0.71", {"start": v(-7.2, -6.2) * mm, "mid": v(-7.06, -6.36) * mm, "end": v(-6.92, -6.5) * mm});
            skLineSegment(sketch, "E175.0.72", {"start": v(-6.92, -6.5) * mm, "end": v(-6.63, -6.52) * mm});
            skArc(sketch, "E175.0.73", {"start": v(-6.63, -6.52) * mm, "mid": v(-6.22, -6.91) * mm, "end": v(-5.8, -7.28) * mm});
            skLineSegment(sketch, "E175.0.74", {"start": v(-5.8, -7.28) * mm, "end": v(-5.74, -7.57) * mm});
            skArc(sketch, "E175.0.75", {"start": v(-5.74, -7.57) * mm, "mid": v(-5.58, -7.69) * mm, "end": v(-5.42, -7.8) * mm});
            skLineSegment(sketch, "E175.0.76", {"start": v(-5.42, -7.8) * mm, "end": v(-5.13, -7.76) * mm});
            skArc(sketch, "E175.0.77", {"start": v(-5.13, -7.76) * mm, "mid": v(-4.65, -8.05) * mm, "end": v(-4.15, -8.32) * mm});
            skLineSegment(sketch, "E175.0.78", {"start": v(-4.15, -8.32) * mm, "end": v(-4.05, -8.6) * mm});
            skArc(sketch, "E175.0.79", {"start": v(-4.05, -8.6) * mm, "mid": v(-3.86, -8.68) * mm, "end": v(-3.68, -8.76) * mm});
            skLineSegment(sketch, "E175.0.80", {"start": v(-3.68, -8.76) * mm, "end": v(-3.4, -8.65) * mm});
            skArc(sketch, "E175.0.81", {"start": v(-3.4, -8.65) * mm, "mid": v(-2.87, -8.84) * mm, "end": v(-2.33, -9) * mm});
            skLineSegment(sketch, "E175.0.82", {"start": v(-2.33, -9) * mm, "end": v(-2.17, -9.25) * mm});
            skArc(sketch, "E175.0.83", {"start": v(-2.17, -9.25) * mm, "mid": v(-1.98, -9.3) * mm, "end": v(-1.78, -9.33) * mm});
            skLineSegment(sketch, "E175.0.84", {"start": v(-1.78, -9.33) * mm, "end": v(-1.53, -9.17) * mm});
            skArc(sketch, "E175.0.85", {"start": v(-1.53, -9.17) * mm, "mid": v(-0.97, -9.25) * mm, "end": v(-0.4, -9.3) * mm});
            skLineSegment(sketch, "E175.0.86", {"start": v(-0.4, -9.3) * mm, "end": v(-0.2, -9.5) * mm});
            skArc(sketch, "E175.0.87", {"start": v(-0.2, -9.5) * mm, "mid": v(0, -9.5) * mm, "end": v(0.2, -9.5) * mm});
            skLineSegment(sketch, "E175.0.88", {"start": v(0.2, -9.5) * mm, "end": v(0.4, -9.3) * mm});
            skArc(sketch, "E175.0.89", {"start": v(0.4, -9.3) * mm, "mid": v(0.97, -9.25) * mm, "end": v(1.53, -9.17) * mm});
            skLineSegment(sketch, "E175.0.90", {"start": v(1.53, -9.17) * mm, "end": v(1.78, -9.33) * mm});
            skArc(sketch, "E175.0.91", {"start": v(1.78, -9.33) * mm, "mid": v(1.98, -9.3) * mm, "end": v(2.17, -9.25) * mm});
            skLineSegment(sketch, "E175.0.92", {"start": v(2.17, -9.25) * mm, "end": v(2.33, -9) * mm});
            skArc(sketch, "E175.0.93", {"start": v(2.33, -9) * mm, "mid": v(2.87, -8.84) * mm, "end": v(3.4, -8.65) * mm});
            skLineSegment(sketch, "E175.0.94", {"start": v(3.4, -8.65) * mm, "end": v(3.68, -8.76) * mm});
            skArc(sketch, "E175.0.95", {"start": v(3.68, -8.76) * mm, "mid": v(3.86, -8.68) * mm, "end": v(4.05, -8.6) * mm});
            skLineSegment(sketch, "E175.0.96", {"start": v(4.05, -8.6) * mm, "end": v(4.15, -8.32) * mm});
            skArc(sketch, "E175.0.97", {"start": v(4.15, -8.32) * mm, "mid": v(4.65, -8.05) * mm, "end": v(5.13, -7.76) * mm});
            skLineSegment(sketch, "E175.0.98", {"start": v(5.13, -7.76) * mm, "end": v(5.42, -7.8) * mm});
            skArc(sketch, "E175.0.99", {"start": v(5.42, -7.8) * mm, "mid": v(5.58, -7.69) * mm, "end": v(5.74, -7.57) * mm});
            skLineSegment(sketch, "E175.0.100", {"start": v(5.74, -7.57) * mm, "end": v(5.8, -7.28) * mm});
            skArc(sketch, "E175.0.101", {"start": v(5.8, -7.28) * mm, "mid": v(6.22, -6.91) * mm, "end": v(6.63, -6.52) * mm});
            skLineSegment(sketch, "E175.0.102", {"start": v(6.63, -6.52) * mm, "end": v(6.92, -6.5) * mm});
            skArc(sketch, "E175.0.103", {"start": v(6.92, -6.5) * mm, "mid": v(7.06, -6.36) * mm, "end": v(7.2, -6.2) * mm});
            skLineSegment(sketch, "E175.0.104", {"start": v(7.2, -6.2) * mm, "end": v(7.18, -5.91) * mm});
            skArc(sketch, "E175.0.105", {"start": v(7.18, -5.91) * mm, "mid": v(7.52, -5.47) * mm, "end": v(7.84, -5) * mm});
            skLineSegment(sketch, "E175.0.106", {"start": v(7.84, -5) * mm, "end": v(8.13, -4.92) * mm});
            skArc(sketch, "E175.0.107", {"start": v(8.13, -4.92) * mm, "mid": v(8.23, -4.75) * mm, "end": v(8.33, -4.58) * mm});
            skLineSegment(sketch, "E175.0.108", {"start": v(8.33, -4.58) * mm, "end": v(8.25, -4.3) * mm});
            skArc(sketch, "E175.0.109", {"start": v(8.25, -4.3) * mm, "mid": v(8.5, -3.78) * mm, "end": v(8.71, -3.26) * mm});
            skLineSegment(sketch, "E175.0.110", {"start": v(8.71, -3.26) * mm, "end": v(8.97, -3.13) * mm});
            skArc(sketch, "E175.0.111", {"start": v(8.97, -3.13) * mm, "mid": v(9.04, -2.94) * mm, "end": v(9.1, -2.74) * mm});
            skLineSegment(sketch, "E175.0.112", {"start": v(9.1, -2.74) * mm, "end": v(8.96, -2.48) * mm});
            skArc(sketch, "E175.0.113", {"start": v(8.96, -2.48) * mm, "mid": v(9.1, -1.93) * mm, "end": v(9.2, -1.38) * mm});
            skLineSegment(sketch, "E175.0.114", {"start": v(9.2, -1.38) * mm, "end": v(9.42, -1.2) * mm});
            skArc(sketch, "E175.0.115", {"start": v(9.42, -1.2) * mm, "mid": v(9.45, -1) * mm, "end": v(9.47, -0.8) * mm});
            skLineSegment(sketch, "E175.0.116", {"start": v(9.47, -0.8) * mm, "end": v(9.28, -0.57) * mm});
            skArc(sketch, "E175.0.117", {"start": v(9.28, -0.57) * mm, "mid": v(9.3, 0) * mm, "end": v(9.28, 0.57) * mm});
            skLineSegment(sketch, "E175.0.118", {"start": v(9.28, 0.57) * mm, "end": v(9.47, 0.8) * mm});
            skArc(sketch, "E175.0.119", {"start": v(9.47, 0.8) * mm, "mid": v(9.45, 1) * mm, "end": v(9.42, 1.2) * mm});
            skSolve(sketch);
        }
        {
            var Q0;
            Q0=makeQuery(id+"F6.imprint","IMPRINT",FACE,{"disambiguationData":[TD([[makeQuery(id+"F6.imprint","IMPRINT",EDGE,{"derivedFrom":sQuery(id+"F6.wireOp",EDGE,"E175.0.0")}),-1.0]])]});
            extrude(context, id + "F7", {"entities" : qUnion([Q0]), "operationType" : NewBodyOperationType.ADD, "depth" : (getVariable(context, 'Bore_Depth_F')) * mm});
        }
        {
            var Q0;
            Q0=makeQuery(id+"F5.opExtrude","CAP_FACE",FACE,{"disambiguationData":[OSD([sQuery(id+"F4.wireOp",EDGE,"E0"),sQuery(id+"F4.wireOp",EDGE,"E1"),sQuery(id+"F4.wireOp",EDGE,"E2"),sQuery(id+"F4.wireOp",EDGE,"E3"),sQuery(id+"F4.wireOp",EDGE,"E4"),sQuery(id+"F4.wireOp",EDGE,"E5"),sQuery(id+"F4.wireOp",EDGE,"E6"),sQuery(id+"F4.wireOp",EDGE,"E7"),sQuery(id+"F4.wireOp",EDGE,"E8"),sQuery(id+"F4.wireOp",EDGE,"E9"),sQuery(id+"F4.wireOp",EDGE,"E10"),sQuery(id+"F4.wireOp",EDGE,"E11"),sQuery(id+"F4.wireOp",EDGE,"E12"),sQuery(id+"F4.wireOp",EDGE,"E13"),sQuery(id+"F4.wireOp",EDGE,"E14"),sQuery(id+"F4.wireOp",EDGE,"E15"),sQuery(id+"F4.wireOp",EDGE,"E16"),sQuery(id+"F4.wireOp",EDGE,"E17"),sQuery(id+"F4.wireOp",EDGE,"E18"),sQuery(id+"F4.wireOp",EDGE,"E19"),sQuery(id+"F4.wireOp",EDGE,"E20"),sQuery(id+"F4.wireOp",EDGE,"E21"),sQuery(id+"F4.wireOp",EDGE,"E22"),sQuery(id+"F4.wireOp",EDGE,"E23"),sQuery(id+"F4.wireOp",EDGE,"E24"),sQuery(id+"F4.wireOp",EDGE,"E25"),sQuery(id+"F4.wireOp",EDGE,"E26"),sQuery(id+"F4.wireOp",EDGE,"E27"),sQuery(id+"F4.wireOp",EDGE,"E28"),sQuery(id+"F4.wireOp",EDGE,"E29"),sQuery(id+"F4.wireOp",EDGE,"E30"),sQuery(id+"F4.wireOp",EDGE,"E31"),sQuery(id+"F4.wireOp",EDGE,"E32"),sQuery(id+"F4.wireOp",EDGE,"E33"),sQuery(id+"F4.wireOp",EDGE,"E34"),sQuery(id+"F4.wireOp",EDGE,"E35"),sQuery(id+"F4.wireOp",EDGE,"E36"),sQuery(id+"F4.wireOp",EDGE,"E37"),sQuery(id+"F4.wireOp",EDGE,"E38"),sQuery(id+"F4.wireOp",EDGE,"E39"),sQuery(id+"F4.wireOp",EDGE,"E40"),sQuery(id+"F4.wireOp",EDGE,"E41"),sQuery(id+"F4.wireOp",EDGE,"E42"),sQuery(id+"F4.wireOp",EDGE,"E43"),sQuery(id+"F4.wireOp",EDGE,"E44"),sQuery(id+"F4.wireOp",EDGE,"E45"),sQuery(id+"F4.wireOp",EDGE,"E46"),sQuery(id+"F4.wireOp",EDGE,"E47"),sQuery(id+"F4.wireOp",EDGE,"E48"),sQuery(id+"F4.wireOp",EDGE,"E49"),sQuery(id+"F4.wireOp",EDGE,"E50"),sQuery(id+"F4.wireOp",EDGE,"E51"),sQuery(id+"F4.wireOp",EDGE,"E52"),sQuery(id+"F4.wireOp",EDGE,"E53"),sQuery(id+"F4.wireOp",EDGE,"E54"),sQuery(id+"F4.wireOp",EDGE,"E55"),sQuery(id+"F4.wireOp",EDGE,"E56"),sQuery(id+"F4.wireOp",EDGE,"E57"),sQuery(id+"F4.wireOp",EDGE,"E58"),sQuery(id+"F4.wireOp",EDGE,"E59"),sQuery(id+"F4.wireOp",EDGE,"E60"),sQuery(id+"F4.wireOp",EDGE,"E61"),sQuery(id+"F4.wireOp",EDGE,"E62"),sQuery(id+"F4.wireOp",EDGE,"E63"),sQuery(id+"F4.wireOp",EDGE,"E64"),sQuery(id+"F4.wireOp",EDGE,"E65"),sQuery(id+"F4.wireOp",EDGE,"E66"),sQuery(id+"F4.wireOp",EDGE,"E67"),sQuery(id+"F4.wireOp",EDGE,"E68"),sQuery(id+"F4.wireOp",EDGE,"E69"),sQuery(id+"F4.wireOp",EDGE,"E70"),sQuery(id+"F4.wireOp",EDGE,"E71"),sQuery(id+"F4.wireOp",EDGE,"E72"),sQuery(id+"F4.wireOp",EDGE,"E73"),sQuery(id+"F4.wireOp",EDGE,"E74"),sQuery(id+"F4.wireOp",EDGE,"E75"),sQuery(id+"F4.wireOp",EDGE,"E76"),sQuery(id+"F4.wireOp",EDGE,"E77"),sQuery(id+"F4.wireOp",EDGE,"E78"),sQuery(id+"F4.wireOp",EDGE,"E79"),sQuery(id+"F4.wireOp",EDGE,"E80"),sQuery(id+"F4.wireOp",EDGE,"E81"),sQuery(id+"F4.wireOp",EDGE,"E82"),sQuery(id+"F4.wireOp",EDGE,"E83"),sQuery(id+"F4.wireOp",EDGE,"E84"),sQuery(id+"F4.wireOp",EDGE,"E85"),sQuery(id+"F4.wireOp",EDGE,"E86"),sQuery(id+"F4.wireOp",EDGE,"E87"),sQuery(id+"F4.wireOp",EDGE,"E88"),sQuery(id+"F4.wireOp",EDGE,"E89"),sQuery(id+"F4.wireOp",EDGE,"E90"),sQuery(id+"F4.wireOp",EDGE,"E91"),sQuery(id+"F4.wireOp",EDGE,"E92"),sQuery(id+"F4.wireOp",EDGE,"E93"),sQuery(id+"F4.wireOp",EDGE,"E94"),sQuery(id+"F4.wireOp",EDGE,"E95"),sQuery(id+"F4.wireOp",EDGE,"E96"),sQuery(id+"F4.wireOp",EDGE,"E97"),sQuery(id+"F4.wireOp",EDGE,"E98"),sQuery(id+"F4.wireOp",EDGE,"E99"),sQuery(id+"F4.wireOp",EDGE,"E100"),sQuery(id+"F4.wireOp",EDGE,"E101"),sQuery(id+"F4.wireOp",EDGE,"E102"),sQuery(id+"F4.wireOp",EDGE,"E103"),sQuery(id+"F4.wireOp",EDGE,"E104"),sQuery(id+"F4.wireOp",EDGE,"E105"),sQuery(id+"F4.wireOp",EDGE,"E106"),sQuery(id+"F4.wireOp",EDGE,"E107"),sQuery(id+"F4.wireOp",EDGE,"E108"),sQuery(id+"F4.wireOp",EDGE,"E109"),sQuery(id+"F4.wireOp",EDGE,"E110"),sQuery(id+"F4.wireOp",EDGE,"E111"),sQuery(id+"F4.wireOp",EDGE,"E112"),sQuery(id+"F4.wireOp",EDGE,"E113"),sQuery(id+"F4.wireOp",EDGE,"E114"),sQuery(id+"F4.wireOp",EDGE,"E115"),sQuery(id+"F4.wireOp",EDGE,"E116"),sQuery(id+"F4.wireOp",EDGE,"E117"),sQuery(id+"F4.wireOp",EDGE,"E118"),sQuery(id+"F4.wireOp",EDGE,"E119"),sQuery(id+"F4.wireOp",EDGE,"E120"),sQuery(id+"F4.wireOp",EDGE,"E121"),sQuery(id+"F4.wireOp",EDGE,"E122"),sQuery(id+"F4.wireOp",EDGE,"E123"),sQuery(id+"F4.wireOp",EDGE,"E124"),sQuery(id+"F4.wireOp",EDGE,"E125"),sQuery(id+"F4.wireOp",EDGE,"E126"),sQuery(id+"F4.wireOp",EDGE,"E127"),sQuery(id+"F4.wireOp",EDGE,"E128"),sQuery(id+"F4.wireOp",EDGE,"E129"),sQuery(id+"F4.wireOp",EDGE,"E130"),sQuery(id+"F4.wireOp",EDGE,"E131"),sQuery(id+"F4.wireOp",EDGE,"E132"),sQuery(id+"F4.wireOp",EDGE,"E133"),sQuery(id+"F4.wireOp",EDGE,"E134"),sQuery(id+"F4.wireOp",EDGE,"E135"),sQuery(id+"F4.wireOp",EDGE,"E136"),sQuery(id+"F4.wireOp",EDGE,"E137"),sQuery(id+"F4.wireOp",EDGE,"E138"),sQuery(id+"F4.wireOp",EDGE,"E139"),sQuery(id+"F4.wireOp",EDGE,"E140"),sQuery(id+"F4.wireOp",EDGE,"E141"),sQuery(id+"F4.wireOp",EDGE,"E142"),sQuery(id+"F4.wireOp",EDGE,"E143"),sQuery(id+"F4.wireOp",EDGE,"E144"),sQuery(id+"F4.wireOp",EDGE,"E145"),sQuery(id+"F4.wireOp",EDGE,"E146"),sQuery(id+"F4.wireOp",EDGE,"E147"),sQuery(id+"F4.wireOp",EDGE,"E148"),sQuery(id+"F4.wireOp",EDGE,"E149"),sQuery(id+"F4.wireOp",EDGE,"E150"),sQuery(id+"F4.wireOp",EDGE,"E151"),sQuery(id+"F4.wireOp",EDGE,"E152"),sQuery(id+"F4.wireOp",EDGE,"E153"),sQuery(id+"F4.wireOp",EDGE,"E154"),sQuery(id+"F4.wireOp",EDGE,"E155"),sQuery(id+"F4.wireOp",EDGE,"E156"),sQuery(id+"F4.wireOp",EDGE,"E157"),sQuery(id+"F4.wireOp",EDGE,"E158"),sQuery(id+"F4.wireOp",EDGE,"E159"),sQuery(id+"F4.wireOp",EDGE,"E160"),sQuery(id+"F4.wireOp",EDGE,"E161"),sQuery(id+"F4.wireOp",EDGE,"E162"),sQuery(id+"F4.wireOp",EDGE,"E163"),sQuery(id+"F4.wireOp",EDGE,"E164"),sQuery(id+"F4.wireOp",EDGE,"E165"),sQuery(id+"F4.wireOp",EDGE,"E166"),sQuery(id+"F4.wireOp",EDGE,"E167"),sQuery(id+"F4.wireOp",EDGE,"E168"),sQuery(id+"F4.wireOp",EDGE,"E169"),sQuery(id+"F4.wireOp",EDGE,"E170"),sQuery(id+"F4.wireOp",EDGE,"E171"),sQuery(id+"F4.wireOp",EDGE,"E172"),sQuery(id+"F4.wireOp",EDGE,"E173")])],"isStart":true});
            var sketch = newSketch(context, id + "F8", { "sketchPlane" : qUnion([Q0])});
            skCircle(sketch, "E176", {"center": v(0, 0) * mm, "radius": 8 * mm});
            skLineSegment(sketch, "E177.0.0", {"start": v(-9.2, 1.38) * mm, "end": v(-9.42, 1.2) * mm});
            skArc(sketch, "E177.0.1", {"start": v(-9.42, 1.2) * mm, "mid": v(-9.45, 1) * mm, "end": v(-9.47, 0.8) * mm});
            skLineSegment(sketch, "E177.0.2", {"start": v(-9.47, 0.8) * mm, "end": v(-9.28, 0.57) * mm});
            skArc(sketch, "E177.0.3", {"start": v(-9.28, 0.57) * mm, "mid": v(-9.3, 0) * mm, "end": v(-9.28, -0.57) * mm});
            skLineSegment(sketch, "E177.0.4", {"start": v(-9.28, -0.57) * mm, "end": v(-9.47, -0.8) * mm});
            skArc(sketch, "E177.0.5", {"start": v(-9.47, -0.8) * mm, "mid": v(-9.45, -1) * mm, "end": v(-9.42, -1.2) * mm});
            skLineSegment(sketch, "E177.0.6", {"start": v(-9.42, -1.2) * mm, "end": v(-9.2, -1.38) * mm});
            skArc(sketch, "E177.0.7", {"start": v(-9.2, -1.38) * mm, "mid": v(-9.1, -1.93) * mm, "end": v(-8.96, -2.48) * mm});
            skLineSegment(sketch, "E177.0.8", {"start": v(-8.96, -2.48) * mm, "end": v(-9.1, -2.74) * mm});
            skArc(sketch, "E177.0.9", {"start": v(-9.1, -2.74) * mm, "mid": v(-9.04, -2.94) * mm, "end": v(-8.97, -3.13) * mm});
            skLineSegment(sketch, "E177.0.10", {"start": v(-8.97, -3.13) * mm, "end": v(-8.71, -3.26) * mm});
            skArc(sketch, "E177.0.11", {"start": v(-8.71, -3.26) * mm, "mid": v(-8.5, -3.78) * mm, "end": v(-8.25, -4.3) * mm});
            skLineSegment(sketch, "E177.0.12", {"start": v(-8.25, -4.3) * mm, "end": v(-8.33, -4.58) * mm});
            skArc(sketch, "E177.0.13", {"start": v(-8.33, -4.58) * mm, "mid": v(-8.23, -4.75) * mm, "end": v(-8.13, -4.92) * mm});
            skLineSegment(sketch, "E177.0.14", {"start": v(-8.13, -4.92) * mm, "end": v(-7.84, -5) * mm});
            skArc(sketch, "E177.0.15", {"start": v(-7.84, -5) * mm, "mid": v(-7.52, -5.47) * mm, "end": v(-7.18, -5.91) * mm});
            skLineSegment(sketch, "E177.0.16", {"start": v(-7.18, -5.91) * mm, "end": v(-7.2, -6.2) * mm});
            skArc(sketch, "E177.0.17", {"start": v(-7.2, -6.2) * mm, "mid": v(-7.06, -6.36) * mm, "end": v(-6.92, -6.5) * mm});
            skLineSegment(sketch, "E177.0.18", {"start": v(-6.92, -6.5) * mm, "end": v(-6.63, -6.52) * mm});
            skArc(sketch, "E177.0.19", {"start": v(-6.63, -6.52) * mm, "mid": v(-6.22, -6.91) * mm, "end": v(-5.8, -7.28) * mm});
            skLineSegment(sketch, "E177.0.20", {"start": v(-5.8, -7.28) * mm, "end": v(-5.74, -7.57) * mm});
            skArc(sketch, "E177.0.21", {"start": v(-5.74, -7.57) * mm, "mid": v(-5.58, -7.69) * mm, "end": v(-5.42, -7.8) * mm});
            skLineSegment(sketch, "E177.0.22", {"start": v(-5.42, -7.8) * mm, "end": v(-5.13, -7.76) * mm});
            skArc(sketch, "E177.0.23", {"start": v(-5.13, -7.76) * mm, "mid": v(-4.65, -8.05) * mm, "end": v(-4.15, -8.32) * mm});
            skLineSegment(sketch, "E177.0.24", {"start": v(-4.15, -8.32) * mm, "end": v(-4.05, -8.6) * mm});
            skArc(sketch, "E177.0.25", {"start": v(-4.05, -8.6) * mm, "mid": v(-3.86, -8.68) * mm, "end": v(-3.68, -8.76) * mm});
            skLineSegment(sketch, "E177.0.26", {"start": v(-3.68, -8.76) * mm, "end": v(-3.4, -8.65) * mm});
            skArc(sketch, "E177.0.27", {"start": v(-3.4, -8.65) * mm, "mid": v(-2.87, -8.84) * mm, "end": v(-2.33, -9) * mm});
            skLineSegment(sketch, "E177.0.28", {"start": v(-2.33, -9) * mm, "end": v(-2.17, -9.25) * mm});
            skArc(sketch, "E177.0.29", {"start": v(-2.17, -9.25) * mm, "mid": v(-1.98, -9.3) * mm, "end": v(-1.78, -9.33) * mm});
            skLineSegment(sketch, "E177.0.30", {"start": v(-1.78, -9.33) * mm, "end": v(-1.53, -9.17) * mm});
            skArc(sketch, "E177.0.31", {"start": v(-1.53, -9.17) * mm, "mid": v(-0.97, -9.25) * mm, "end": v(-0.4, -9.3) * mm});
            skLineSegment(sketch, "E177.0.32", {"start": v(-0.4, -9.3) * mm, "end": v(-0.2, -9.5) * mm});
            skArc(sketch, "E177.0.33", {"start": v(-0.2, -9.5) * mm, "mid": v(0, -9.5) * mm, "end": v(0.2, -9.5) * mm});
            skLineSegment(sketch, "E177.0.34", {"start": v(0.2, -9.5) * mm, "end": v(0.4, -9.3) * mm});
            skArc(sketch, "E177.0.35", {"start": v(0.4, -9.3) * mm, "mid": v(0.97, -9.25) * mm, "end": v(1.53, -9.17) * mm});
            skLineSegment(sketch, "E177.0.36", {"start": v(1.53, -9.17) * mm, "end": v(1.78, -9.33) * mm});
            skArc(sketch, "E177.0.37", {"start": v(1.78, -9.33) * mm, "mid": v(1.98, -9.3) * mm, "end": v(2.17, -9.25) * mm});
            skLineSegment(sketch, "E177.0.38", {"start": v(2.17, -9.25) * mm, "end": v(2.33, -9) * mm});
            skArc(sketch, "E177.0.39", {"start": v(2.33, -9) * mm, "mid": v(2.87, -8.84) * mm, "end": v(3.4, -8.65) * mm});
            skLineSegment(sketch, "E177.0.40", {"start": v(3.4, -8.65) * mm, "end": v(3.68, -8.76) * mm});
            skArc(sketch, "E177.0.41", {"start": v(3.68, -8.76) * mm, "mid": v(3.86, -8.68) * mm, "end": v(4.05, -8.6) * mm});
            skLineSegment(sketch, "E177.0.42", {"start": v(4.05, -8.6) * mm, "end": v(4.15, -8.32) * mm});
            skArc(sketch, "E177.0.43", {"start": v(4.15, -8.32) * mm, "mid": v(4.65, -8.05) * mm, "end": v(5.13, -7.76) * mm});
            skLineSegment(sketch, "E177.0.44", {"start": v(5.13, -7.76) * mm, "end": v(5.42, -7.8) * mm});
            skArc(sketch, "E177.0.45", {"start": v(5.42, -7.8) * mm, "mid": v(5.58, -7.69) * mm, "end": v(5.74, -7.57) * mm});
            skLineSegment(sketch, "E177.0.46", {"start": v(5.74, -7.57) * mm, "end": v(5.8, -7.28) * mm});
            skArc(sketch, "E177.0.47", {"start": v(5.8, -7.28) * mm, "mid": v(6.22, -6.91) * mm, "end": v(6.63, -6.52) * mm});
            skLineSegment(sketch, "E177.0.48", {"start": v(6.63, -6.52) * mm, "end": v(6.92, -6.5) * mm});
            skArc(sketch, "E177.0.49", {"start": v(6.92, -6.5) * mm, "mid": v(7.06, -6.36) * mm, "end": v(7.2, -6.2) * mm});
            skLineSegment(sketch, "E177.0.50", {"start": v(7.2, -6.2) * mm, "end": v(7.18, -5.91) * mm});
            skArc(sketch, "E177.0.51", {"start": v(7.18, -5.91) * mm, "mid": v(7.52, -5.47) * mm, "end": v(7.84, -5) * mm});
            skLineSegment(sketch, "E177.0.52", {"start": v(7.84, -5) * mm, "end": v(8.13, -4.92) * mm});
            skArc(sketch, "E177.0.53", {"start": v(8.13, -4.92) * mm, "mid": v(8.23, -4.75) * mm, "end": v(8.33, -4.58) * mm});
            skLineSegment(sketch, "E177.0.54", {"start": v(8.33, -4.58) * mm, "end": v(8.25, -4.3) * mm});
            skArc(sketch, "E177.0.55", {"start": v(8.25, -4.3) * mm, "mid": v(8.5, -3.78) * mm, "end": v(8.71, -3.26) * mm});
            skLineSegment(sketch, "E177.0.56", {"start": v(8.71, -3.26) * mm, "end": v(8.97, -3.13) * mm});
            skArc(sketch, "E177.0.57", {"start": v(8.97, -3.13) * mm, "mid": v(9.04, -2.94) * mm, "end": v(9.1, -2.74) * mm});
            skLineSegment(sketch, "E177.0.58", {"start": v(9.1, -2.74) * mm, "end": v(8.96, -2.48) * mm});
            skArc(sketch, "E177.0.59", {"start": v(8.96, -2.48) * mm, "mid": v(9.1, -1.93) * mm, "end": v(9.2, -1.38) * mm});
            skLineSegment(sketch, "E177.0.60", {"start": v(9.2, -1.38) * mm, "end": v(9.42, -1.2) * mm});
            skArc(sketch, "E177.0.61", {"start": v(9.42, -1.2) * mm, "mid": v(9.45, -1) * mm, "end": v(9.47, -0.8) * mm});
            skLineSegment(sketch, "E177.0.62", {"start": v(9.47, -0.8) * mm, "end": v(9.28, -0.57) * mm});
            skArc(sketch, "E177.0.63", {"start": v(9.28, -0.57) * mm, "mid": v(9.3, 0) * mm, "end": v(9.28, 0.57) * mm});
            skLineSegment(sketch, "E177.0.64", {"start": v(9.28, 0.57) * mm, "end": v(9.47, 0.8) * mm});
            skArc(sketch, "E177.0.65", {"start": v(9.47, 0.8) * mm, "mid": v(9.45, 1) * mm, "end": v(9.42, 1.2) * mm});
            skLineSegment(sketch, "E177.0.66", {"start": v(9.42, 1.2) * mm, "end": v(9.2, 1.38) * mm});
            skArc(sketch, "E177.0.67", {"start": v(9.2, 1.38) * mm, "mid": v(9.1, 1.93) * mm, "end": v(8.96, 2.48) * mm});
            skLineSegment(sketch, "E177.0.68", {"start": v(8.96, 2.48) * mm, "end": v(9.1, 2.74) * mm});
            skArc(sketch, "E177.0.69", {"start": v(9.1, 2.74) * mm, "mid": v(9.04, 2.94) * mm, "end": v(8.97, 3.13) * mm});
            skLineSegment(sketch, "E177.0.70", {"start": v(8.97, 3.13) * mm, "end": v(8.71, 3.26) * mm});
            skArc(sketch, "E177.0.71", {"start": v(8.71, 3.26) * mm, "mid": v(8.5, 3.78) * mm, "end": v(8.25, 4.3) * mm});
            skLineSegment(sketch, "E177.0.72", {"start": v(8.25, 4.3) * mm, "end": v(8.33, 4.58) * mm});
            skArc(sketch, "E177.0.73", {"start": v(8.33, 4.58) * mm, "mid": v(8.23, 4.75) * mm, "end": v(8.13, 4.92) * mm});
            skLineSegment(sketch, "E177.0.74", {"start": v(8.13, 4.92) * mm, "end": v(7.84, 5) * mm});
            skArc(sketch, "E177.0.75", {"start": v(7.84, 5) * mm, "mid": v(7.52, 5.47) * mm, "end": v(7.18, 5.91) * mm});
            skLineSegment(sketch, "E177.0.76", {"start": v(7.18, 5.91) * mm, "end": v(7.2, 6.2) * mm});
            skArc(sketch, "E177.0.77", {"start": v(7.2, 6.2) * mm, "mid": v(7.06, 6.36) * mm, "end": v(6.92, 6.5) * mm});
            skLineSegment(sketch, "E177.0.78", {"start": v(6.92, 6.5) * mm, "end": v(6.63, 6.52) * mm});
            skArc(sketch, "E177.0.79", {"start": v(6.63, 6.52) * mm, "mid": v(6.22, 6.91) * mm, "end": v(5.8, 7.28) * mm});
            skLineSegment(sketch, "E177.0.80", {"start": v(5.8, 7.28) * mm, "end": v(5.74, 7.57) * mm});
            skArc(sketch, "E177.0.81", {"start": v(5.74, 7.57) * mm, "mid": v(5.58, 7.69) * mm, "end": v(5.42, 7.8) * mm});
            skLineSegment(sketch, "E177.0.82", {"start": v(5.42, 7.8) * mm, "end": v(5.13, 7.76) * mm});
            skArc(sketch, "E177.0.83", {"start": v(5.13, 7.76) * mm, "mid": v(4.65, 8.05) * mm, "end": v(4.15, 8.32) * mm});
            skLineSegment(sketch, "E177.0.84", {"start": v(4.15, 8.32) * mm, "end": v(4.05, 8.6) * mm});
            skArc(sketch, "E177.0.85", {"start": v(4.05, 8.6) * mm, "mid": v(3.86, 8.68) * mm, "end": v(3.68, 8.76) * mm});
            skLineSegment(sketch, "E177.0.86", {"start": v(3.68, 8.76) * mm, "end": v(3.4, 8.65) * mm});
            skArc(sketch, "E177.0.87", {"start": v(3.4, 8.65) * mm, "mid": v(2.87, 8.84) * mm, "end": v(2.33, 9) * mm});
            skLineSegment(sketch, "E177.0.88", {"start": v(2.33, 9) * mm, "end": v(2.17, 9.25) * mm});
            skArc(sketch, "E177.0.89", {"start": v(2.17, 9.25) * mm, "mid": v(1.98, 9.3) * mm, "end": v(1.78, 9.33) * mm});
            skLineSegment(sketch, "E177.0.90", {"start": v(1.78, 9.33) * mm, "end": v(1.53, 9.17) * mm});
            skArc(sketch, "E177.0.91", {"start": v(1.53, 9.17) * mm, "mid": v(0.97, 9.25) * mm, "end": v(0.4, 9.3) * mm});
            skLineSegment(sketch, "E177.0.92", {"start": v(0.4, 9.3) * mm, "end": v(0.2, 9.5) * mm});
            skArc(sketch, "E177.0.93", {"start": v(0.2, 9.5) * mm, "mid": v(0, 9.5) * mm, "end": v(-0.2, 9.5) * mm});
            skLineSegment(sketch, "E177.0.94", {"start": v(-0.2, 9.5) * mm, "end": v(-0.4, 9.3) * mm});
            skArc(sketch, "E177.0.95", {"start": v(-0.4, 9.3) * mm, "mid": v(-0.97, 9.25) * mm, "end": v(-1.53, 9.17) * mm});
            skLineSegment(sketch, "E177.0.96", {"start": v(-1.53, 9.17) * mm, "end": v(-1.78, 9.33) * mm});
            skArc(sketch, "E177.0.97", {"start": v(-1.78, 9.33) * mm, "mid": v(-1.98, 9.3) * mm, "end": v(-2.17, 9.25) * mm});
            skLineSegment(sketch, "E177.0.98", {"start": v(-2.17, 9.25) * mm, "end": v(-2.33, 9) * mm});
            skArc(sketch, "E177.0.99", {"start": v(-2.33, 9) * mm, "mid": v(-2.87, 8.84) * mm, "end": v(-3.4, 8.65) * mm});
            skLineSegment(sketch, "E177.0.100", {"start": v(-3.4, 8.65) * mm, "end": v(-3.68, 8.76) * mm});
            skArc(sketch, "E177.0.101", {"start": v(-3.68, 8.76) * mm, "mid": v(-3.86, 8.68) * mm, "end": v(-4.05, 8.6) * mm});
            skLineSegment(sketch, "E177.0.102", {"start": v(-4.05, 8.6) * mm, "end": v(-4.15, 8.32) * mm});
            skArc(sketch, "E177.0.103", {"start": v(-4.15, 8.32) * mm, "mid": v(-4.65, 8.05) * mm, "end": v(-5.13, 7.76) * mm});
            skLineSegment(sketch, "E177.0.104", {"start": v(-5.13, 7.76) * mm, "end": v(-5.42, 7.8) * mm});
            skArc(sketch, "E177.0.105", {"start": v(-5.42, 7.8) * mm, "mid": v(-5.58, 7.69) * mm, "end": v(-5.74, 7.57) * mm});
            skLineSegment(sketch, "E177.0.106", {"start": v(-5.74, 7.57) * mm, "end": v(-5.8, 7.28) * mm});
            skArc(sketch, "E177.0.107", {"start": v(-5.8, 7.28) * mm, "mid": v(-6.22, 6.91) * mm, "end": v(-6.63, 6.52) * mm});
            skLineSegment(sketch, "E177.0.108", {"start": v(-6.63, 6.52) * mm, "end": v(-6.92, 6.5) * mm});
            skArc(sketch, "E177.0.109", {"start": v(-6.92, 6.5) * mm, "mid": v(-7.06, 6.36) * mm, "end": v(-7.2, 6.2) * mm});
            skLineSegment(sketch, "E177.0.110", {"start": v(-7.2, 6.2) * mm, "end": v(-7.18, 5.91) * mm});
            skArc(sketch, "E177.0.111", {"start": v(-7.18, 5.91) * mm, "mid": v(-7.52, 5.47) * mm, "end": v(-7.84, 5) * mm});
            skLineSegment(sketch, "E177.0.112", {"start": v(-7.84, 5) * mm, "end": v(-8.13, 4.92) * mm});
            skArc(sketch, "E177.0.113", {"start": v(-8.13, 4.92) * mm, "mid": v(-8.23, 4.75) * mm, "end": v(-8.33, 4.58) * mm});
            skLineSegment(sketch, "E177.0.114", {"start": v(-8.33, 4.58) * mm, "end": v(-8.25, 4.3) * mm});
            skArc(sketch, "E177.0.115", {"start": v(-8.25, 4.3) * mm, "mid": v(-8.5, 3.78) * mm, "end": v(-8.71, 3.26) * mm});
            skLineSegment(sketch, "E177.0.116", {"start": v(-8.71, 3.26) * mm, "end": v(-8.97, 3.13) * mm});
            skArc(sketch, "E177.0.117", {"start": v(-8.97, 3.13) * mm, "mid": v(-9.04, 2.94) * mm, "end": v(-9.1, 2.74) * mm});
            skLineSegment(sketch, "E177.0.118", {"start": v(-9.1, 2.74) * mm, "end": v(-8.96, 2.48) * mm});
            skArc(sketch, "E177.0.119", {"start": v(-8.96, 2.48) * mm, "mid": v(-9.1, 1.93) * mm, "end": v(-9.2, 1.38) * mm});
            skSolve(sketch);
        }
        {
            var Q0;
            Q0=makeQuery(id+"F8.imprint","IMPRINT",FACE,{"disambiguationData":[TD([[makeQuery(id+"F8.imprint","IMPRINT",EDGE,{"derivedFrom":sQuery(id+"F8.wireOp",EDGE,"E177.0.0")}),1.0]])]});
            extrude(context, id + "F9", {"entities" : qUnion([Q0]), "operationType" : NewBodyOperationType.ADD, "depth" : (getVariable(context, 'Bore_Depth_R')) * mm});
        }
        {
            var Q0;
            Q0=qCreatedBy(makeId("Right.planeOp"),FACE);
            cPlane(context, id + "F10", {"entities" : qUnion([Q0]), "cplaneType" : CPlaneType.OFFSET, "offset" : (getVariable(context, 'Main_Diam')) / 2 * mm, "oppositeDirection" : true, "width" : 150 * mm, "height" : 150 * mm});
        }
        {
            var Q0;
            Q0=qCreatedBy(id+"F10.planeOp",FACE);
            var sketch = newSketch(context, id + "F11", { "sketchPlane" : qUnion([Q0])});
            skCircle(sketch, "E178", {"center": v(-277, 0) * mm, "radius": 1.25 * mm});
            skPoint(sketch, "E179", {"position": v(-56.13, 0) * mm});
            skCircle(sketch, "E180", {"center": v(-268, 0) * mm, "radius": 3.25 * mm});
            skSolve(sketch);
        }
        {
            var Q0;
            Q0=makeQuery(id+"F11.imprint","IMPRINT",FACE,{"disambiguationData":[TD([[makeQuery(id+"F11.imprint","IMPRINT",EDGE,{"derivedFrom":sQuery(id+"F11.wireOp",EDGE,"E178")}),1.0]])]});
            var Q1;
            Q1=makeQuery(id+"F11.imprint","IMPRINT",FACE,{"disambiguationData":[TD([[makeQuery(id+"F11.imprint","IMPRINT",EDGE,{"derivedFrom":sQuery(id+"F11.wireOp",EDGE,"E180")}),1.0]])]});
            extrude(context, id + "F12", {"entities" : qUnion([Q0, Q1]), "operationType" : NewBodyOperationType.REMOVE, "depth" : 5 * mm});
        }
    });
